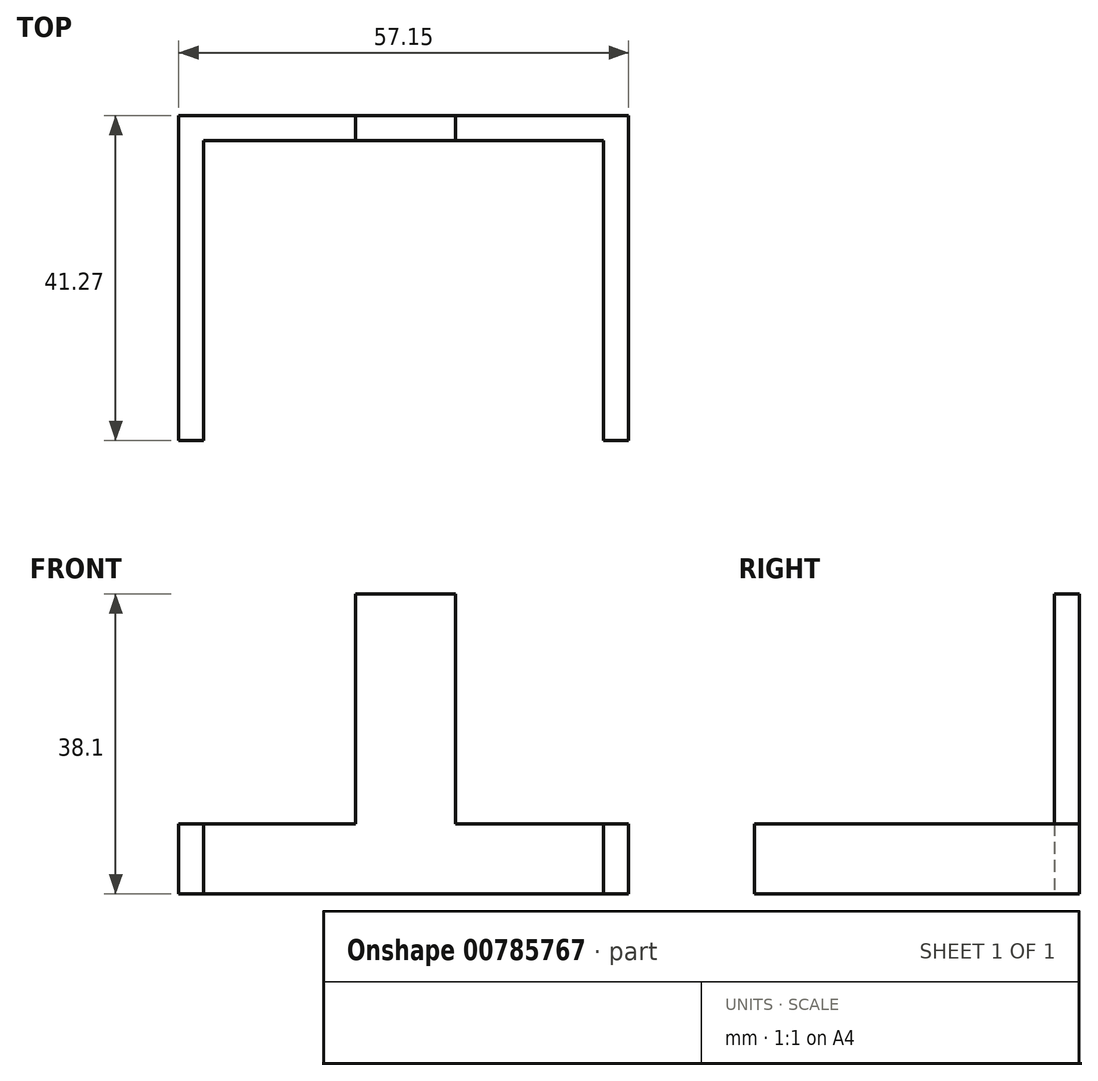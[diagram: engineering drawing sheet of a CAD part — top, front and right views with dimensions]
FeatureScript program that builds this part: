
annotation { "Feature Type Name" : "Feature", "Feature Type Description" : "" }
export const myFeature = defineFeature(function(context is Context, id is Id, definition is map)
    precondition{}
    {
        {
            var Q0;
            Q0=qCreatedBy(makeId("Front.planeOp"),FACE);
            var sketch = newSketch(context, id + "F0", { "sketchPlane" : qUnion([Q0])});
            skLineSegment(sketch, "E0.bottom", {"start": v(6.35, -19.05) * mm, "end": v(-6.35, -19.05) * mm});
            skLineSegment(sketch, "E0.top", {"start": v(6.35, 19.05) * mm, "end": v(-6.35, 19.05) * mm});
            skLineSegment(sketch, "E0.left", {"start": v(6.35, -19.05) * mm, "end": v(6.35, 19.05) * mm});
            skLineSegment(sketch, "E0.right", {"start": v(-6.35, -19.05) * mm, "end": v(-6.35, 19.05) * mm});
            skPoint(sketch, "E0.middle", {"position": v(0, 0) * mm});
            skSolve(sketch);
        }
        {
            var Q0;
            Q0=qSketchRegion(id+"F0",true);
            extrude(context, id + "F1", {"entities" : qUnion([Q0]), "depth" : 3.17 * mm, "offsetDistance" : 25.4 * mm});
        }
        {
            var Q0;
            Q0=makeQuery(id+"F1.opExtrude","CAP_FACE",FACE,{"disambiguationData":[OSD([sQuery(id+"F0.wireOp",EDGE,"E0.bottom"),sQuery(id+"F0.wireOp",EDGE,"E0.top"),sQuery(id+"F0.wireOp",EDGE,"E0.left"),sQuery(id+"F0.wireOp",EDGE,"E0.right")])],"isStart":false});
            var sketch = newSketch(context, id + "F2", { "sketchPlane" : qUnion([Q0])});
            skLineSegment(sketch, "E1.bottom", {"start": v(6.35, -19.05) * mm, "end": v(-4.69, -19.05) * mm});
            skLineSegment(sketch, "E1.top", {"start": v(3.86, -10.16) * mm, "end": v(-6.35, -10.16) * mm});
            skPoint(sketch, "E2", {"position": v(-5.52, -14.6) * mm});
            skPoint(sketch, "E3", {"position": v(5.1, -14.6) * mm});
            skPoint(sketch, "E4", {"position": v(-0.2, -14.6) * mm});
            skLineSegment(sketch, "E5.bottom", {"start": v(28.37, -19.05) * mm, "end": v(-28.78, -19.05) * mm});
            skLineSegment(sketch, "E5.top", {"start": v(28.37, -10.16) * mm, "end": v(-28.78, -10.16) * mm});
            skLineSegment(sketch, "E5.left", {"start": v(28.37, -19.05) * mm, "end": v(28.37, -10.16) * mm});
            skLineSegment(sketch, "E5.right", {"start": v(-28.78, -19.05) * mm, "end": v(-28.78, -10.16) * mm});
            skSolve(sketch);
        }
        {
            var Q0;
            Q0=qSketchRegion(id+"F2",true);
            extrude(context, id + "F3", {"entities" : qUnion([Q0]), "operationType" : NewBodyOperationType.ADD, "oppositeDirection" : true, "depth" : 3.17 * mm, "offsetDistance" : 25.4 * mm});
        }
        {
            var Q0;
            Q0=makeQuery(id+"F3.boolean.opBoolean","MERGE",FACE,{"derivedFrom":[makeQuery(id+"F1.opExtrude","CAP_FACE",FACE,{"disambiguationData":[OSD([sQuery(id+"F0.wireOp",EDGE,"E0.bottom"),sQuery(id+"F0.wireOp",EDGE,"E0.top"),sQuery(id+"F0.wireOp",EDGE,"E0.left"),sQuery(id+"F0.wireOp",EDGE,"E0.right")])],"isStart":false}),makeQuery(id+"F3.opExtrude","CAP_FACE",FACE,{"disambiguationData":[OSD([sQuery(id+"F2.wireOp",EDGE,"E5.bottom"),sQuery(id+"F2.wireOp",EDGE,"E5.top"),sQuery(id+"F2.wireOp",EDGE,"E5.left"),sQuery(id+"F2.wireOp",EDGE,"E5.right")])],"isStart":true})]});
            var sketch = newSketch(context, id + "F4", { "sketchPlane" : qUnion([Q0])});
            skLineSegment(sketch, "E6.bottom", {"start": v(-28.78, -10.16) * mm, "end": v(-25.6, -10.16) * mm});
            skLineSegment(sketch, "E6.top", {"start": v(-28.78, -19.05) * mm, "end": v(-25.6, -19.05) * mm});
            skLineSegment(sketch, "E6.left", {"start": v(-28.78, -10.16) * mm, "end": v(-28.78, -19.05) * mm});
            skLineSegment(sketch, "E6.right", {"start": v(-25.6, -10.16) * mm, "end": v(-25.6, -19.05) * mm});
            skLineSegment(sketch, "E7.bottom", {"start": v(28.37, -10.16) * mm, "end": v(25.2, -10.16) * mm});
            skLineSegment(sketch, "E7.top", {"start": v(28.37, -19.05) * mm, "end": v(25.2, -19.05) * mm});
            skLineSegment(sketch, "E7.left", {"start": v(28.37, -10.16) * mm, "end": v(28.37, -19.05) * mm});
            skLineSegment(sketch, "E7.right", {"start": v(25.2, -10.16) * mm, "end": v(25.2, -19.05) * mm});
            skSolve(sketch);
        }
        {
            var Q0;
            Q0=makeQuery(id+"F4.imprint","IMPRINT",FACE,{"disambiguationData":[TD([[makeQuery(id+"F4.imprint","IMPRINT",EDGE,{"derivedFrom":sQuery(id+"F4.wireOp",EDGE,"E6.bottom")}),1.0]])]});
            var Q1;
            Q1=makeQuery(id+"F4.imprint","IMPRINT",FACE,{"disambiguationData":[TD([[makeQuery(id+"F4.imprint","IMPRINT",EDGE,{"derivedFrom":sQuery(id+"F4.wireOp",EDGE,"E7.bottom")}),1.0]])]});
            extrude(context, id + "F5", {"entities" : qUnion([Q0, Q1]), "operationType" : NewBodyOperationType.ADD, "depth" : 38.1 * mm, "offsetDistance" : 25.4 * mm});
        }
    });
